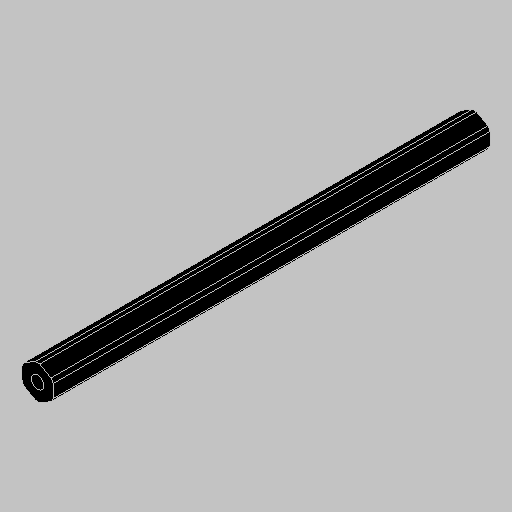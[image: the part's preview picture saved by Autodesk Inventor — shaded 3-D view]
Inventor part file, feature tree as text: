
AUTODESK INVENTOR PART (.ipt)
format: ipt  version: 2023.5 (Build 275446000, 446)  size: 118,272 bytes
history: native  units: in
note: dims shown in document units (in); Inventor stores cm internally (conversion verified against a paired STEP export)
features: extrude x2, projected_geometry x2, hole x1
ambient origin geometry x8: Origin, YZ Plane, XZ Plane, XY Plane, X Axis, Y Axis, Z Axis, Center Point
bodies: Solid1 (feature_tree)
feature tree (5):
  extrude  "Extrusion1"  TaperAngle=0.0deg  [1 undecoded]
  hole  "Hole1"  [1 undecoded]
  extrude  "Extrusion3"  TaperAngle=0.0deg  [1 undecoded]
  projected_geometry  "Project Cut Edges1"
  projected_geometry  "Project Cut Edges2"
note: 3 required parameter values undecoded (feature->parameter linkage not recoverable at this tier; creation-order binding heuristic only, values carry confidence <= 0.55)
